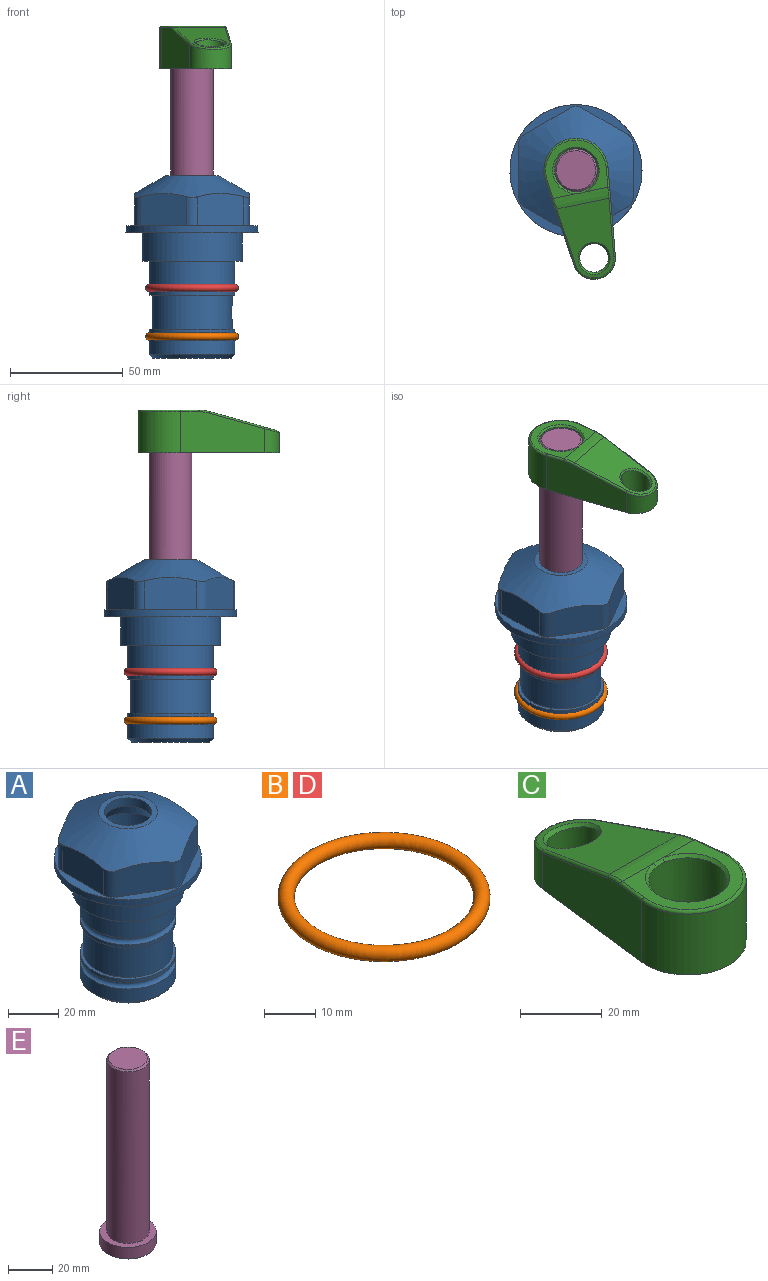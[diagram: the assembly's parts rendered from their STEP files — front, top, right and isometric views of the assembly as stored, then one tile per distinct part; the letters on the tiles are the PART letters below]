
ASSEMBLY  parts=5 mates=4
PART A: 36 faces, bbox 58.7x58.7x81 mm
  f0: cylinder r=17.78mm len=35.56mm, axis (0,0,1), area 1670.8mm2, adj f23,f24,f31
  f1: cylinder r=19.05mm len=38.1mm, axis (0,0,1), area 1191.9mm2, adj f26,f27,f30
  f2: plane 58.66x58.66mm, normal (0,0,-1), area 1150.6mm2, adj f3,f28
  f3: cylinder r=29.33mm len=58.66mm, axis (0,0,-1), area 585.1mm2, adj f2,f4
  f4: plane 58.66x58.66mm, normal (0,0,1), area 475.9mm2, adj f3,f5,f6,f7,f8,f9,f10,f11
  f5: plane 20.32x14.34mm, normal (-0.5,0.87,0), area 324.4mm2, adj f4,f15,f16,f17
  f6: plane 20.32x14.34mm, normal (0.5,0.87,0), area 324.4mm2, adj f4,f14,f15,f17
  f7: plane 23.48x14.34mm, normal (1,0,0), area 324.4mm2, adj f4,f13,f14,f17
  f8: plane 20.32x14.34mm, normal (0.5,-0.87,0), area 324.4mm2, adj f4,f12,f13,f17
  f9: plane 20.32x14.34mm, normal (-0.5,-0.87,0), area 324.4mm2, adj f4,f11,f12,f17
  f10: plane 23.48x14.34mm, normal (-1,0,0), area 324.4mm2, adj f4,f11,f16,f17
  f11: cylinder r=5.08mm len=12.85mm, axis (0,0,-1), area 67.2mm2, adj f4,f9,f10,f17
  f12: cylinder r=5.08mm len=12.85mm, axis (0,0,-1), area 67.2mm2, adj f4,f8,f9,f17
  f13: cylinder r=5.08mm len=12.85mm, axis (0,0,-1), area 67.2mm2, adj f4,f7,f8,f17
  f14: cylinder r=5.08mm len=12.85mm, axis (0,0,-1), area 67.2mm2, adj f4,f6,f7,f17
  f15: cylinder r=5.08mm len=12.85mm, axis (0,0,-1), area 67.2mm2, adj f4,f5,f6,f17
  f16: cylinder r=5.08mm len=12.85mm, axis (0,0,-1), area 67.2mm2, adj f4,f5,f10,f17
  f17: cone r=11.73mm half-angle=60deg, axis (0,0,-1), area 2071.8mm2, adj f5,f6,f7,f8,f9,f10,f11,f12
  f18: plane 23.46x23.46mm, normal (0,0,1), area 147.4mm2, adj f17,f35
  f19: plane 34.93x34.93mm, normal (0,0,-1), area 958mm2, adj f29
  f20: cylinder r=19.05mm len=38.1mm, axis (0,0,1), area 760.1mm2, adj f21,f29
  f21: torus R=19.05mm, axis (0,0,1), area 565.3mm2, adj f20,f22
  f22: cylinder r=19.05mm len=38.1mm, axis (0,0,1), area 190mm2, adj f21,f23
  f23: plane 38.1x38.1mm, normal (0,0,1), area 146.9mm2, adj f0,f22
  f24: plane 38.1x38.1mm, normal (0,0,-1), area 146.9mm2, adj f0,f25
  f25: cylinder r=19.05mm len=38.1mm, axis (0,0,1), area 190mm2, adj f24,f26
  f26: torus R=19.05mm, axis (0,0,1), area 565.3mm2, adj f1,f25
  f27: plane 44.45x44.45mm, normal (0,0,-1), area 411.7mm2, adj f1,f28
  f28: cylinder r=22.23mm len=44.45mm, axis (0,0,1), area 1773.5mm2, adj f2,f27
  f29: cone r=19.05mm half-angle=45deg, axis (0,0,1), area 257.5mm2, adj f19,f20
  f30: cylinder r=3.17mm len=6.75mm, axis (-1,0,0), area 128mm2, adj f1,f33
  f31: cylinder r=3.17mm len=6.35mm, axis (-1,0,0), area 102.5mm2, adj f0,f33
  f32: plane 25.4x25.4mm, normal (0,0,1), area 506.7mm2, adj f33
  f33: cylinder r=12.7mm len=66.42mm, axis (0,0,-1), area 5236.2mm2, adj f30,f31,f32,f34
  f34: cone r=9.53mm half-angle=30deg, axis (0,0,-1), area 443.4mm2, adj f33,f35
  f35: cylinder r=9.53mm len=19.05mm, axis (0,0,-1), area 240.9mm2, adj f18,f34
PART B: 1 faces, bbox 44.7x44.7x3.2 mm
  f0: torus R=19.05mm, axis (0,0,1), area 1193.9mm2
PART C: 31 faces, bbox 31.7x65.5x19.8 mm
  f0: plane 39.12x18.26mm, normal (0.99,0.12,0), area 612.2mm2, adj f1,f4,f7,f11,f13,f15
  f1: cylinder r=9.53mm len=18.91mm, axis (0,0,-1), area 296.1mm2, adj f0,f2,f7,f17
  f2: plane 39.12x18.26mm, normal (-0.99,0.12,0), area 612.2mm2, adj f1,f4,f7,f12,f14,f16
  f3: cylinder r=6.35mm len=12.7mm, axis (0,0,-1), area 362.4mm2, adj f7,f18
  f4: cylinder r=14.29mm len=28.58mm, axis (0,0,-1), area 882.2mm2, adj f0,f2,f7,f10
  f5: cylinder r=9.53mm len=19.05mm, axis (0,0,-1), area 1092.6mm2, adj f7,f19,f20
  f6: plane 26.99x23.69mm, normal (0,0,1), area 216.2mm2, adj f9,f10,f11,f12,f19
  f7: plane 63.5x28.58mm, normal (0,0,-1), area 661.8mm2, adj f0,f1,f2,f3,f4,f5,f22,f23
  f8: plane 33.52x23.6mm, normal (0,0.26,0.97), area 486mm2, adj f9,f15,f16,f17,f18
  f9: cylinder r=19.05mm len=24.72mm, axis (1,0,0), area 120.4mm2, adj f6,f8,f13,f14,f20
  f10: torus R=13.49mm, axis (0,0,1), area 59mm2, adj f4,f6,f11,f12
  f11: cylinder r=0.79mm len=8.67mm, axis (0.12,-0.99,0), area 10.8mm2, adj f0,f6,f10,f13
  f12: cylinder r=0.79mm len=8.67mm, axis (0.12,0.99,0), area 10.8mm2, adj f2,f6,f10,f14
  f13: bspline ~4.95x1.42mm, area 6.1mm2, adj f0,f9,f11,f15
  f14: bspline ~4.95x1.42mm, area 6.1mm2, adj f2,f9,f12,f16
  f15: cylinder r=0.79mm len=25.95mm, axis (0.12,-0.96,0.26), area 32.9mm2, adj f0,f8,f13,f17
  f16: cylinder r=0.79mm len=25.95mm, axis (0.12,0.96,-0.26), area 32.9mm2, adj f2,f8,f14,f17
  f17: bspline ~18.91x8.38mm, area 30mm2, adj f1,f8,f15,f16
  f18: bspline ~14.29x14.29mm, area 48.3mm2, adj f3,f8
  f19: cone r=9.53mm half-angle=45deg, axis (0,0,1), area 66.5mm2, adj f5,f6,f20
  f20: bspline ~3.22x0.96mm, area 3.5mm2, adj f5,f9,f19
  f21: plane 2.75x2.72mm, normal (0,0,-1), area 2.9mm2, adj f23,f25,f28
  f22: plane 23.05x15.88mm, normal (-0.99,-0.12,0), area 323.6mm2, adj f7,f25,f26,f27,f28,f29
  f23: plane 23.05x15.88mm, normal (0.99,-0.12,0), area 323.6mm2, adj f7,f21,f25,f27,f28,f30
  f24: cylinder r=9.53mm len=10.69mm, axis (0,0,-1), area 114.7mm2, adj f7,f27,f29,f30
  f25: cylinder r=12.7mm len=20.59mm, axis (0,0,-1), area 381.1mm2, adj f7,f21,f22,f23,f26,f28
  f26: plane 2.75x2.72mm, normal (0,0,-1), area 2.9mm2, adj f22,f25,f28
  f27: plane 19.72x18.37mm, normal (0,-0.26,-0.97), area 291.8mm2, adj f22,f23,f24,f28,f29,f30
  f28: cylinder r=15.88mm len=19.92mm, axis (1,0,0), area 54.8mm2, adj f21,f22,f23,f25,f26,f27
  f29: cylinder r=1.59mm len=11mm, axis (0,0,-1), area 34.7mm2, adj f7,f22,f24,f27
  f30: cylinder r=1.59mm len=11mm, axis (0,0,-1), area 34.7mm2, adj f7,f23,f24,f27
PART D: same geometry as B
PART E: 6 faces, bbox 25.4x25.4x101.6 mm
  f0: plane 17.46x17.46mm, normal (0,0,1), area 239.5mm2, adj f5
  f1: plane 25.4x25.4mm, normal (0,0,-1), area 506.7mm2, adj f2
  f2: cylinder r=12.7mm len=25.4mm, axis (0,0,1), area 506.7mm2, adj f1,f3
  f3: plane 25.4x25.4mm, normal (0,0,1), area 221.7mm2, adj f2,f4
  f4: cylinder r=9.53mm len=94.46mm, axis (0,0,1), area 5653mm2, adj f3,f5
  f5: cone r=8.73mm half-angle=45deg, axis (0,0,-1), area 64.4mm2, adj f0,f4
PLACE A at identity fixed
PLACE B t=(0,0,-21.59)mm
PLACE C rot(axis=(0,0,-1),168.3deg) t=(0,0,28.35)mm
PLACE D at identity
PLACE E rot(axis=(0,0,-1),168.3deg) t=(0,0,27.55)mm
MATE fastened B.f0 <-> A.f0  axis (0,0,1) through (0,0,-46.1)mm
MATE fastened D.f0 <-> A.f0  axis (0,0,1) through (0,0,-24.51)mm
MATE cylindrical A.f0 <-> E.f2  axis (0,0,1) through (0,0,-50.55)mm
MATE fastened E.f2 <-> C.f4  axis (0,0,1) through (0,0,91.05)mm
